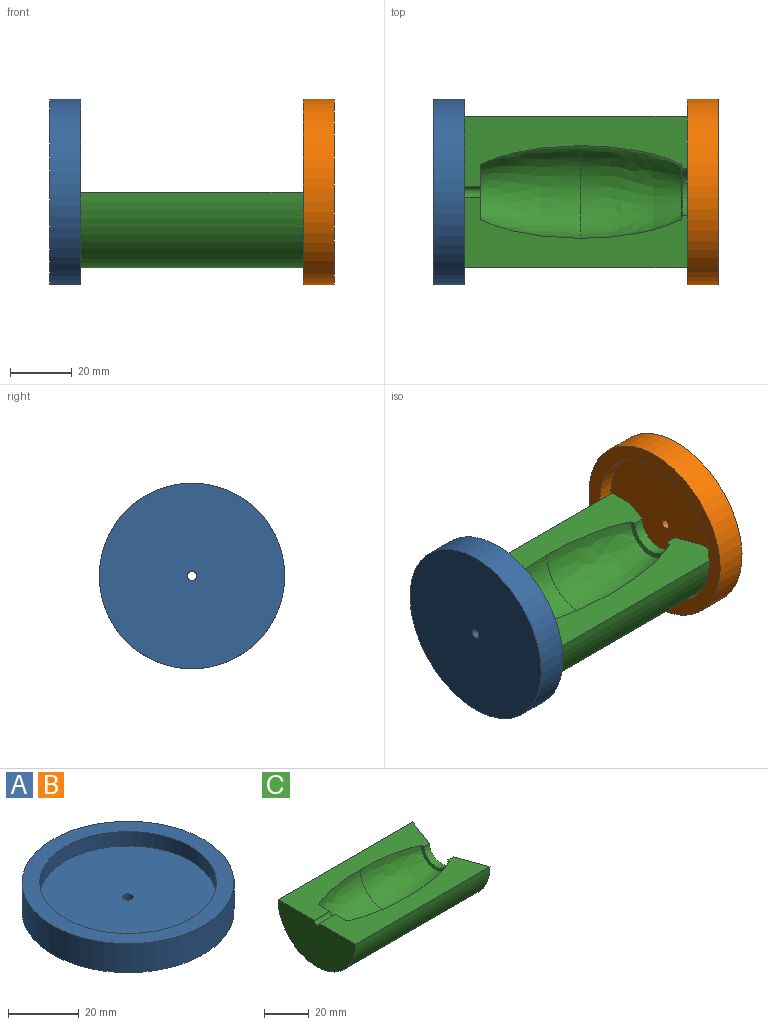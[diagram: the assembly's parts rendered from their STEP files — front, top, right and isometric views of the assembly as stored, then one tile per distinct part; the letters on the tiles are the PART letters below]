
ASSEMBLY  parts=3 mates=2
PART A: 6 faces, bbox 60x60x10 mm
  f0: cylinder r=1.5mm len=5mm, axis (0,0,-1), area 47.1mm2, adj f3,f5
  f1: cylinder r=30mm len=60mm, axis (0,0,-1), area 1885mm2, adj f2,f3
  f2: plane 60x60mm, normal (0,0,1), area 863.9mm2, adj f1,f4
  f3: plane 60x60mm, normal (0,0,-1), area 2820.4mm2, adj f0,f1
  f4: cylinder r=25mm len=50mm, axis (0,0,1), area 785.4mm2, adj f2,f5
  f5: plane 50x50mm, normal (0,0,1), area 1956.4mm2, adj f0,f4
PART B: same geometry as A
PART C: 11 faces, bbox 85x49x24.5 mm
  f0: cylinder r=7.5mm len=15mm, axis (-1,0,0), area 80.9mm2, adj f1,f8,f9,f10
  f1: cone r=8.91mm half-angle=75deg, axis (-1,0,0), area 37.7mm2, adj f0,f2,f9,f10
  f2: revolved ~32.5x30mm, area 1374mm2, adj f1,f3,f9,f10
  f3: revolved ~32.5x30mm, area 1374.1mm2, adj f2,f4,f9,f10
  f4: plane 17.82x8.91mm, normal (1,0,0), area 120.5mm2, adj f3,f5,f9,f10
  f5: cylinder r=1.65mm len=10mm, axis (-1,0,0), area 51.8mm2, adj f4,f6,f9,f10
  f6: plane 49x24.5mm, normal (-1,0,0), area 938.6mm2, adj f5,f7,f9,f10
  f7: cylinder r=24.5mm len=85mm, axis (-1,0,0), area 6542.4mm2, adj f6,f8,f9,f10
  f8: cone r=7.5mm half-angle=70deg, axis (1,0,0), area 909.4mm2, adj f0,f7,f9,f10
  f9: plane 85x22.85mm, normal (0,0,1), area 1082mm2, adj f0,f1,f2,f3,f4,f5,f6,f7
  f10: plane 85x22.85mm, normal (0,0,1), area 1082mm2, adj f0,f1,f2,f3,f4,f5,f6,f7
PLACE A rot(axis=(-0.71,0,-0.71),180deg) t=(-58.81,7.75,14.96)mm
PLACE B rot(axis=(0.71,0,-0.71),180deg) t=(33.1,7.75,14.96)mm
PLACE C t=(-11.31,-7.25,14.96)mm
MATE fastened B.f4 <-> C.f0  axis (-1,0,0) through (28.1,7.75,14.96)mm
MATE fastened A.f4 <-> C.f0  axis (1,0,0) through (-53.81,7.75,14.96)mm
